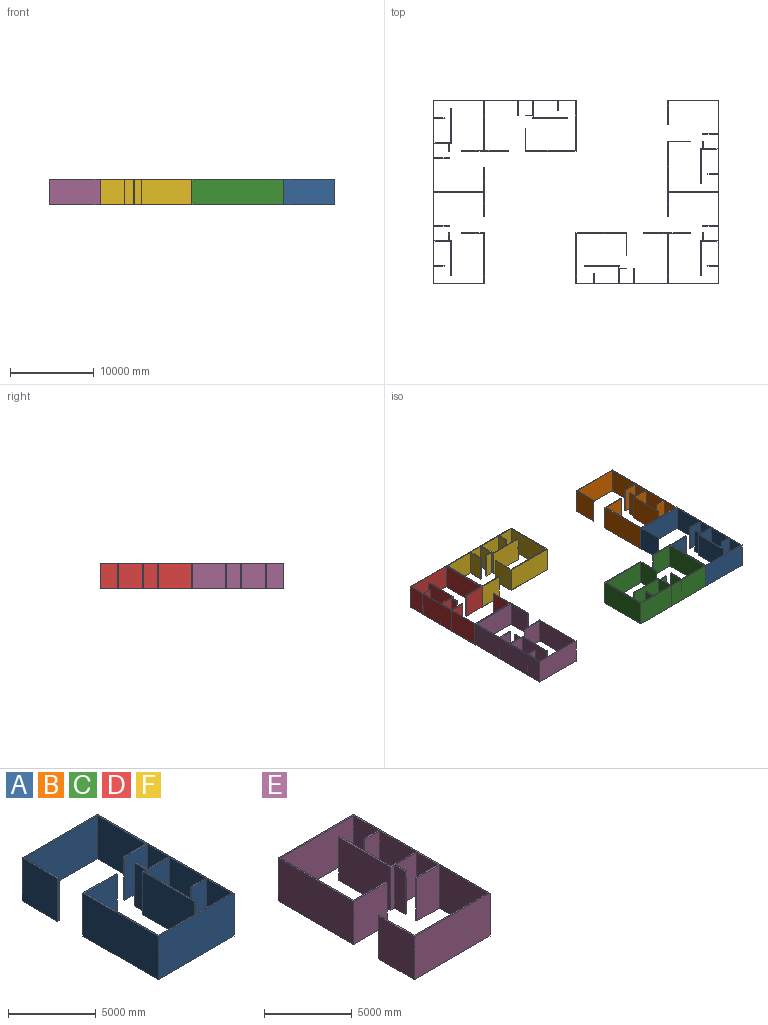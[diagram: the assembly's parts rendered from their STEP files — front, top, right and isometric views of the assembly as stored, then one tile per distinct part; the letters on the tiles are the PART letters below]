
ASSEMBLY  parts=6 mates=15
PART A: 34 faces, bbox 6100x11000x3000 mm
  f0: plane 3000x2000mm, normal (0,-1,0), area 6000000mm2, adj f1,f31,f32,f33
  f1: plane 3000x2900mm, normal (-1,0,0), area 8700000mm2, adj f0,f2,f32,f33
  f2: plane 3000x1200mm, normal (0,1,0), area 3600000mm2, adj f1,f3,f32,f33
  f3: plane 3000x100mm, normal (-1,0,0), area 300000mm2, adj f2,f4,f32,f33
  f4: plane 3000x1200mm, normal (0,-1,0), area 3600000mm2, adj f3,f5,f32,f33
  f5: plane 3000x2000mm, normal (-1,0,0), area 6000000mm2, adj f4,f6,f32,f33
  f6: plane 5900x3000mm, normal (0,1,0), area 17700000mm2, adj f5,f7,f32,f33
  f7: plane 5900x3000mm, normal (1,0,0), area 17700000mm2, adj f6,f8,f32,f33
  f8: plane 3000x2600mm, normal (0,-1,0), area 7800000mm2, adj f7,f9,f32,f33
  f9: plane 3000x100mm, normal (1,0,0), area 300000mm2, adj f8,f10,f32,f33
  f10: plane 3000x2700mm, normal (0,1,0), area 8100000mm2, adj f9,f11,f32,f33
  f11: plane 6100x3000mm, normal (-1,0,0), area 18300000mm2, adj f10,f12,f32,f33
  f12: plane 6100x3000mm, normal (0,-1,0), area 18300000mm2, adj f11,f13,f32,f33
  f13: plane 11000x3000mm, normal (1,0,0), area 33000000mm2, adj f12,f14,f32,f33
  f14: plane 6100x3000mm, normal (0,1,0), area 18300000mm2, adj f13,f15,f32,f33
  f15: plane 3000x2900mm, normal (-1,0,0), area 8700000mm2, adj f14,f16,f32,f33
  f16: plane 3000x100mm, normal (0,-1,0), area 300000mm2, adj f15,f17,f32,f33
  f17: plane 3000x2800mm, normal (1,0,0), area 8400000mm2, adj f16,f18,f32,f33
  f18: plane 5900x3000mm, normal (0,-1,0), area 17700000mm2, adj f17,f19,f32,f33
  f19: plane 3900x3000mm, normal (-1,0,0), area 11700000mm2, adj f18,f20,f32,f33
  f20: plane 3000x1800mm, normal (0,1,0), area 5400000mm2, adj f19,f21,f32,f33
  f21: plane 3000x100mm, normal (-1,0,0), area 300000mm2, adj f20,f22,f32,f33
  f22: plane 3000x1800mm, normal (0,-1,0), area 5400000mm2, adj f21,f23,f32,f33
  f23: plane 3000x1700mm, normal (-1,0,0), area 5100000mm2, adj f22,f24,f32,f33
  f24: plane 3000x1700mm, normal (0,1,0), area 5100000mm2, adj f23,f25,f32,f33
  f25: plane 3000x900mm, normal (1,0,0), area 2700000mm2, adj f24,f26,f32,f33
  f26: plane 3000x100mm, normal (0,1,0), area 300000mm2, adj f25,f27,f32,f33
  f27: plane 3000x900mm, normal (-1,0,0), area 2700000mm2, adj f26,f28,f32,f33
  f28: plane 3000x300mm, normal (0,1,0), area 900000mm2, adj f27,f29,f32,f33
  f29: plane 4200x3000mm, normal (-1,0,0), area 12600000mm2, adj f28,f30,f32,f33
  f30: plane 3000x100mm, normal (0,-1,0), area 300000mm2, adj f29,f31,f32,f33
  f31: plane 4100x3000mm, normal (1,0,0), area 12300000mm2, adj f0,f30,f32,f33
  f32: plane 11000x6100mm, normal (0,0,1), area 4450000mm2, adj f0,f1,f2,f3,f4,f5,f6,f7
  f33: plane 11000x6100mm, normal (0,0,-1), area 4450000mm2, adj f0,f1,f2,f3,f4,f5,f6,f7
PART B: same geometry as A
PART C: same geometry as A
PART D: same geometry as A
PART E: 34 faces, bbox 6100x11000x3000 mm
  f0: plane 3000x900mm, normal (-1,0,0), area 2700000mm2, adj f1,f31,f32,f33
  f1: plane 3000x100mm, normal (0,-1,0), area 300000mm2, adj f0,f2,f32,f33
  f2: plane 3000x900mm, normal (1,0,0), area 2700000mm2, adj f1,f3,f32,f33
  f3: plane 3000x1700mm, normal (0,-1,0), area 5100000mm2, adj f2,f4,f32,f33
  f4: plane 3000x1700mm, normal (-1,0,0), area 5100000mm2, adj f3,f5,f32,f33
  f5: plane 3000x1800mm, normal (0,1,0), area 5400000mm2, adj f4,f6,f32,f33
  f6: plane 3000x100mm, normal (-1,0,0), area 300000mm2, adj f5,f7,f32,f33
  f7: plane 3000x1800mm, normal (0,-1,0), area 5400000mm2, adj f6,f8,f32,f33
  f8: plane 3900x3000mm, normal (-1,0,0), area 11700000mm2, adj f7,f9,f32,f33
  f9: plane 5900x3000mm, normal (0,1,0), area 17700000mm2, adj f8,f10,f32,f33
  f10: plane 3000x2800mm, normal (1,0,0), area 8400000mm2, adj f9,f11,f32,f33
  f11: plane 3000x100mm, normal (0,1,0), area 300000mm2, adj f10,f12,f32,f33
  f12: plane 3000x2900mm, normal (-1,0,0), area 8700000mm2, adj f11,f13,f32,f33
  f13: plane 6100x3000mm, normal (0,-1,0), area 18300000mm2, adj f12,f14,f32,f33
  f14: plane 11000x3000mm, normal (1,0,0), area 33000000mm2, adj f13,f15,f32,f33
  f15: plane 6100x3000mm, normal (0,1,0), area 18300000mm2, adj f14,f16,f32,f33
  f16: plane 6100x3000mm, normal (-1,0,0), area 18300000mm2, adj f15,f17,f32,f33
  f17: plane 3000x2700mm, normal (0,-1,0), area 8100000mm2, adj f16,f18,f32,f33
  f18: plane 3000x100mm, normal (1,0,0), area 300000mm2, adj f17,f19,f32,f33
  f19: plane 3000x2600mm, normal (0,1,0), area 7800000mm2, adj f18,f20,f32,f33
  f20: plane 5900x3000mm, normal (1,0,0), area 17700000mm2, adj f19,f21,f32,f33
  f21: plane 5900x3000mm, normal (0,-1,0), area 17700000mm2, adj f20,f22,f32,f33
  f22: plane 3000x2000mm, normal (-1,0,0), area 6000000mm2, adj f21,f23,f32,f33
  f23: plane 3000x1200mm, normal (0,1,0), area 3600000mm2, adj f22,f24,f32,f33
  f24: plane 3000x100mm, normal (-1,0,0), area 300000mm2, adj f23,f25,f32,f33
  f25: plane 3000x1200mm, normal (0,-1,0), area 3600000mm2, adj f24,f26,f32,f33
  f26: plane 3000x2900mm, normal (-1,0,0), area 8700000mm2, adj f25,f27,f32,f33
  f27: plane 3000x2000mm, normal (0,1,0), area 6000000mm2, adj f26,f28,f32,f33
  f28: plane 4100x3000mm, normal (1,0,0), area 12300000mm2, adj f27,f29,f32,f33
  f29: plane 3000x100mm, normal (0,1,0), area 300000mm2, adj f28,f30,f32,f33
  f30: plane 4200x3000mm, normal (-1,0,0), area 12600000mm2, adj f29,f31,f32,f33
  f31: plane 3000x300mm, normal (0,-1,0), area 900000mm2, adj f0,f30,f32,f33
  f32: plane 11000x6100mm, normal (0,0,1), area 4450000mm2, adj f0,f1,f2,f3,f4,f5,f6,f7
  f33: plane 11000x6100mm, normal (0,0,-1), area 4450000mm2, adj f0,f1,f2,f3,f4,f5,f6,f7
PART F: same geometry as A
PLACE A t=(-3003.38,13352.82,0)mm
PLACE B t=(-3003.38,24352.82,0)mm
PLACE C rot(axis=(0,0,-1),90deg) t=(-11497.18,10953.38,0)mm
PLACE D rot(axis=(0,0,-1),180deg) t=(-30996.62,24347.18,0)mm
PLACE E rot(axis=(0,0,1),180deg) t=(-31220.44,12284.85,0)mm
PLACE F rot(axis=(0,0,1),90deg) t=(-22502.82,26746.62,0)mm
MATE planar D.f32 <-> E.f32  axis (0,0,1) through (-31431.57,24660.67,3000)mm
MATE planar F.f14 <-> D.f11  axis (-1,0,0) through (-28000,26800,1500)mm
MATE planar C.f13 <-> A.f12  axis (0,-1,0) through (-6000,7850,3000)mm
MATE planar C.f32 <-> A.f32  axis (0,0,1) through (-6000,7850,3000)mm
MATE planar D.f14 <-> E.f13  axis (0,-1,0) through (-31050,18850,1500)mm
MATE planar C.f14 <-> A.f11  axis (1,0,0) through (-6000,7850,3000)mm
MATE planar B.f12 <-> A.f14  axis (0,-1,0) through (100,18850,3000)mm
MATE planar E.f33 <-> C.f33  axis (0,0,-1) through (-31431.57,13039.33,0)mm
MATE planar B.f14 <-> F.f13  axis (0,1,0) through (-2950,29850,1500)mm
MATE planar D.f13 <-> E.f14  axis (-1,0,0) through (-34100,18850,3000)mm
MATE planar C.f12 <-> F.f12  axis (-1,0,0) through (-17000,10900,1500)mm
MATE planar F.f32 <-> D.f32  axis (0,0,1) through (-22189.33,27181.57,3000)mm
MATE planar B.f32 <-> A.f32  axis (0,0,1) through (100,18850,3000)mm
MATE planar F.f13 <-> D.f12  axis (0,1,0) through (-22500,29850,1500)mm
MATE planar B.f13 <-> A.f13  axis (1,0,0) through (100,18850,3000)mm
